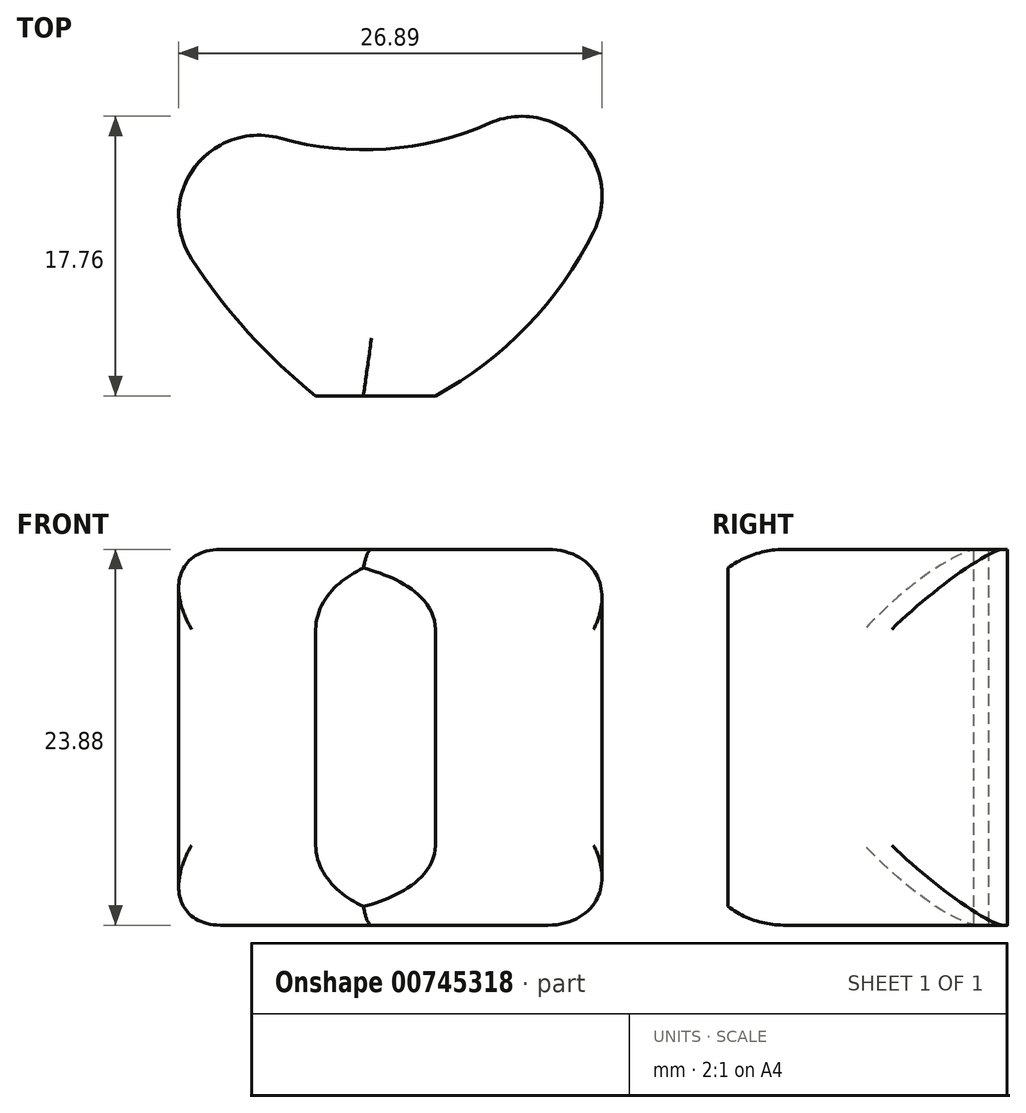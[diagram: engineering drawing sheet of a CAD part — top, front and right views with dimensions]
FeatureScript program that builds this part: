
annotation { "Feature Type Name" : "Feature", "Feature Type Description" : "" }
export const myFeature = defineFeature(function(context is Context, id is Id, definition is map)
    precondition{}
    {
        {
            var Q0;
            Q0=qCreatedBy(makeId("Top.planeOp"),FACE);
            var sketch = newSketch(context, id + "F0", { "sketchPlane" : qUnion([Q0])});
            skArc(sketch, "E0", {"start": v(-50.45, 0) * mm, "mid": v(-33.67, -9.4) * mm, "end": v(-16.89, 0) * mm});
            skArc(sketch, "E1", {"start": v(-50.45, 0) * mm, "mid": v(-46.08, -13.87) * mm, "end": v(-36.73, -25.02) * mm});
            skArc(sketch, "E2", {"start": v(-29.13, -25.02) * mm, "mid": v(-19.01, -14.47) * mm, "end": v(-16.89, 0) * mm});
            skLineSegment(sketch, "E3", {"start": v(-36.73, -25.02) * mm, "end": v(-29.13, -25.02) * mm});
            skSolve(sketch);
        }
        {
            var Q0;
            Q0 = qSketchRegion(id + "F0", true);
            extrude(context, id + "F1", {"entities" : qUnion([Q0]), "oppositeDirection" : true, "depth" : 23.88 * mm, "offsetDistance" : 25.4 * mm});
        }
        {
            var Q0;
            Q0=makeQuery(id+"F1.opExtrude","CAP_EDGE",EDGE,{"disambiguationData":[OSD([sQuery(id+"F0.wireOp",EDGE,"E1")])],"isStart":true});
            var Q1;
            Q1=makeQuery(id+"F1.opExtrude","CAP_EDGE",EDGE,{"disambiguationData":[OSD([sQuery(id+"F0.wireOp",EDGE,"E2")])],"isStart":true});
            var Q2;
            Q2=makeQuery(id+"F1.opExtrude","CAP_EDGE",EDGE,{"disambiguationData":[OSD([sQuery(id+"F0.wireOp",EDGE,"E2")])],"isStart":false});
            var Q3;
            Q3=makeQuery(id+"F1.opExtrude","CAP_EDGE",EDGE,{"disambiguationData":[OSD([sQuery(id+"F0.wireOp",EDGE,"E1")])],"isStart":false});
            var Q4;
            Q4=makeQuery(id+"F1.opExtrude","SWEPT_EDGE",EDGE,{"disambiguationData":[OSD([sQuery(id+"F0.wireOp",EDGE,"E0"),sQuery(id+"F0.wireOp",EDGE,"E1")])]});
            var Q5;
            Q5=makeQuery(id+"F1.opExtrude","SWEPT_EDGE",EDGE,{"disambiguationData":[OSD([sQuery(id+"F0.wireOp",EDGE,"E0"),sQuery(id+"F0.wireOp",EDGE,"E2")])]});
            fillet(context, id + "F2", {"entities" : qUnion([Q0, Q1, Q2, Q3, Q4, Q5]), "radius" : 5.08 * mm, "tangentPropagation" : true, "allowEdgeOverflow" : false});
        }
    });
